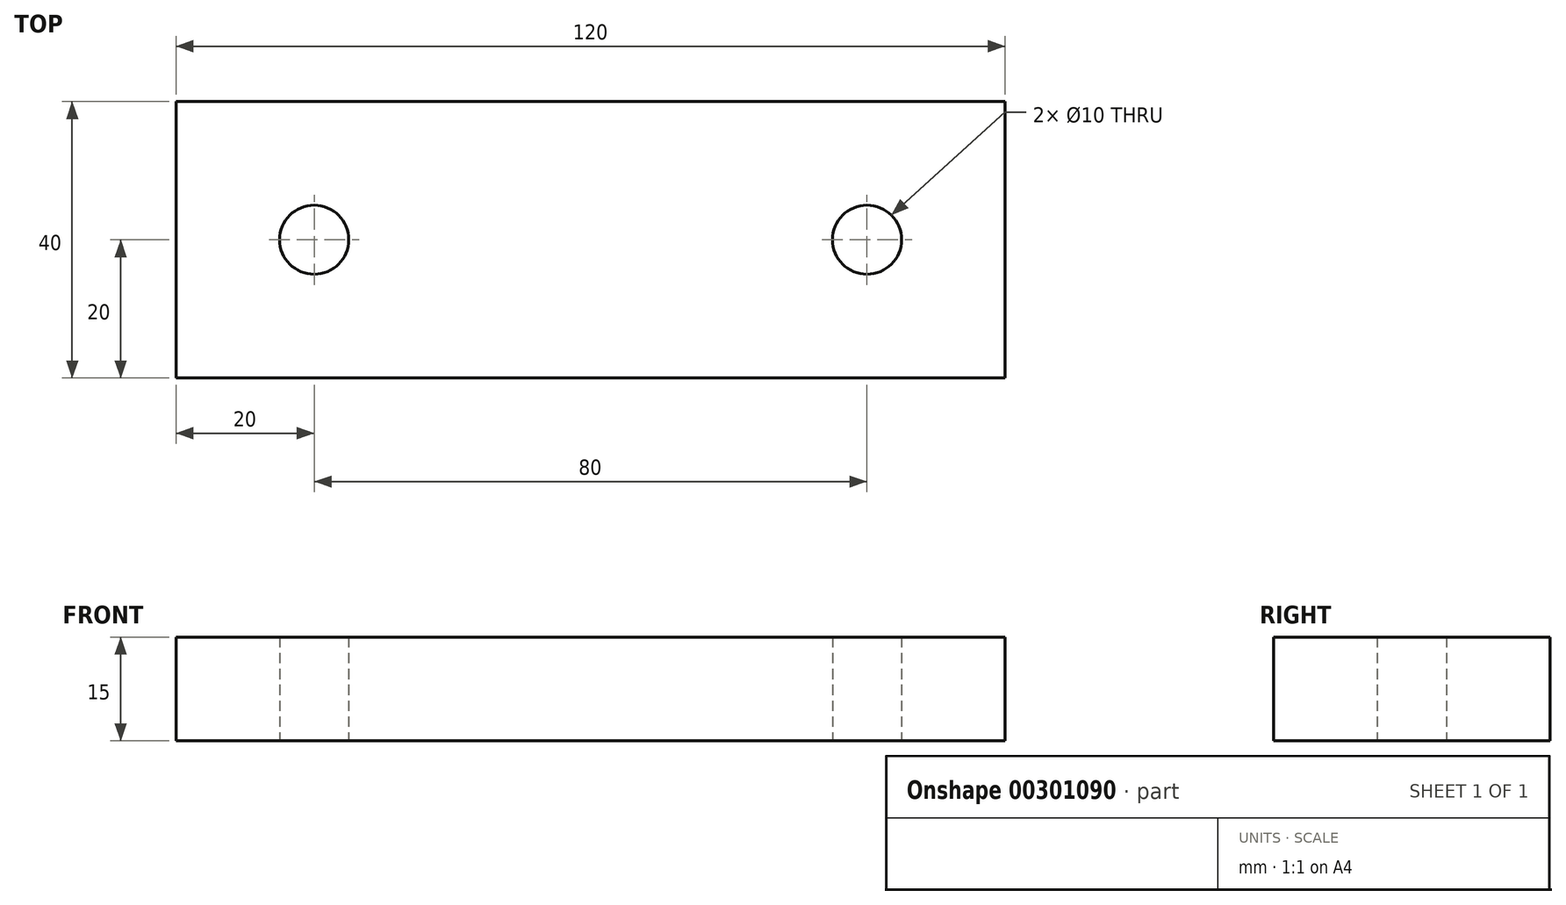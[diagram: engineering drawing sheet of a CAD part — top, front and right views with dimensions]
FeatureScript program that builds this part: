
annotation { "Feature Type Name" : "Feature", "Feature Type Description" : "" }
export const myFeature = defineFeature(function(context is Context, id is Id, definition is map)
    precondition{}
    {
        {
            var Q0;
            Q0=qCreatedBy(makeId("Top.planeOp"),FACE);
            var sketch = newSketch(context, id + "F0", { "sketchPlane" : qUnion([Q0])});
            skLineSegment(sketch, "E0", {"start": v(0, 0) * mm, "end": v(0, 40) * mm});
            skLineSegment(sketch, "E1", {"start": v(0, 40) * mm, "end": v(120, 40) * mm});
            skLineSegment(sketch, "E2", {"start": v(120, 40) * mm, "end": v(120, 0) * mm});
            skLineSegment(sketch, "E3", {"start": v(120, 0) * mm, "end": v(0, 0) * mm});
            skCircle(sketch, "E4", {"center": v(20, 20) * mm, "radius": 5 * mm});
            skCircle(sketch, "E5", {"center": v(100, 20) * mm, "radius": 5 * mm});
            skSolve(sketch);
        }
        {
            var Q0;
            Q0 = qSketchRegion(id + "F0", true);
            extrude(context, id + "F1", {"entities" : qUnion([Q0]), "endBound" : BoundingType.SYMMETRIC, "depth" : 15 * mm});
        }
    });
